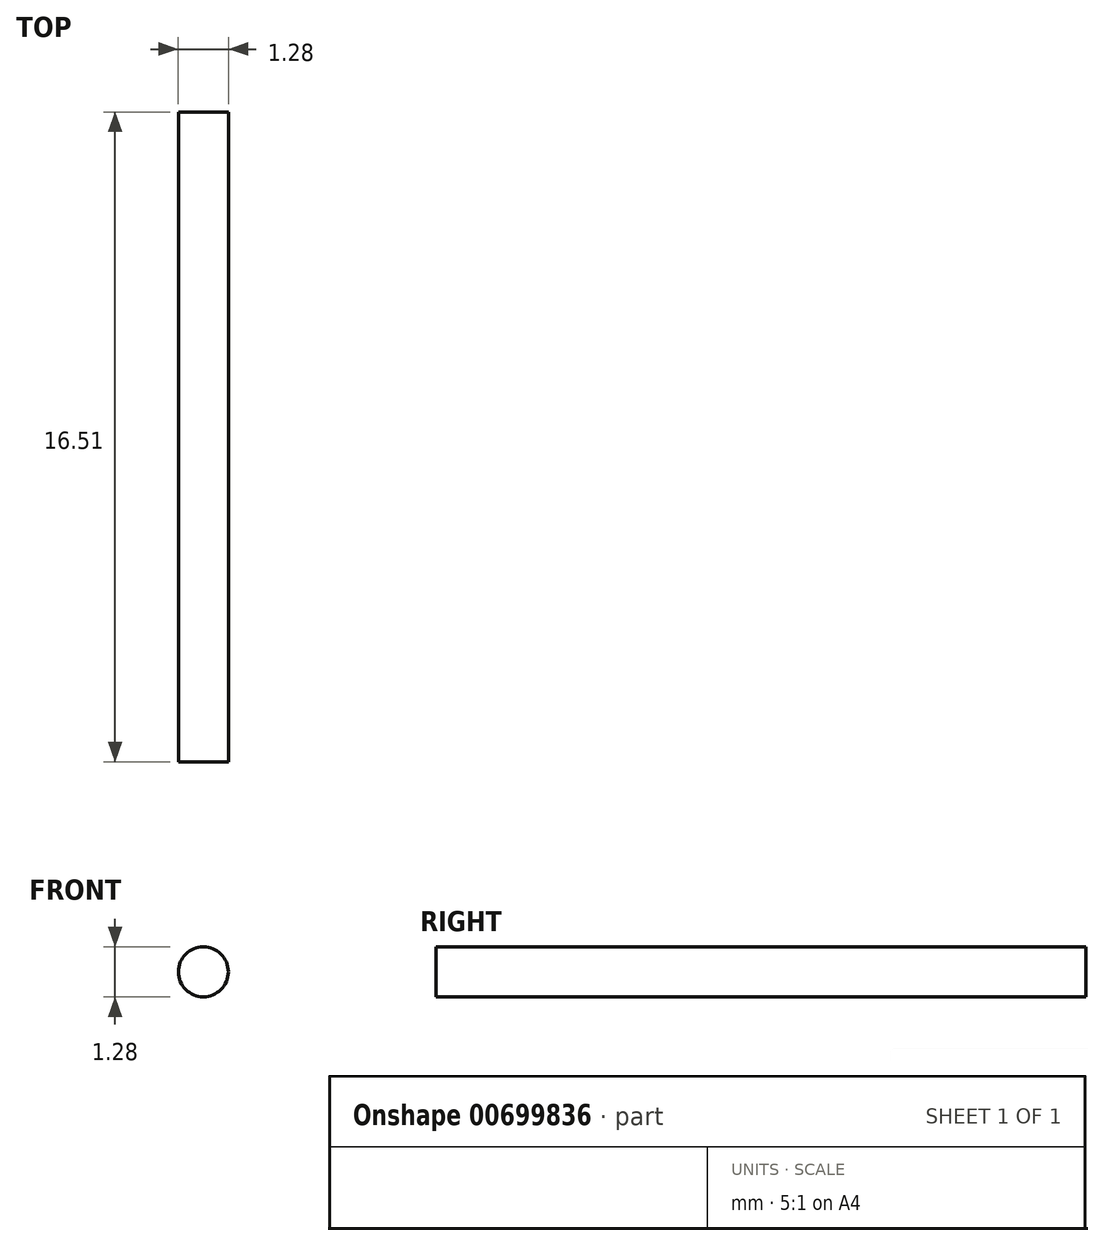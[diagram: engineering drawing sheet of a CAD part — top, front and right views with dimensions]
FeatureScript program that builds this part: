
annotation { "Feature Type Name" : "Feature", "Feature Type Description" : "" }
export const myFeature = defineFeature(function(context is Context, id is Id, definition is map)
    precondition{}
    {
        {
            var Q0;
            Q0=qCreatedBy(makeId("Front.planeOp"),FACE);
            var sketch = newSketch(context, id + "F0", { "sketchPlane" : qUnion([Q0])});
            skCircle(sketch, "E0", {"center": v(0, 0) * mm, "radius": 0.64 * mm});
            skSolve(sketch);
        }
        {
            var Q0;
            Q0=qSketchRegion(id+"F0",true);
            extrude(context, id + "F1", {"entities" : qUnion([Q0]), "depth" : 16.5 * mm});
        }
    });
